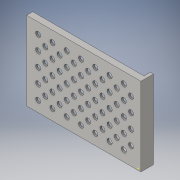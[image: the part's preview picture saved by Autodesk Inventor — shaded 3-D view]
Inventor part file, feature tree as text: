
AUTODESK INVENTOR PART (.ipt)
format: ipt  version: 2016 (Build 200138000, 138)  size: 350,208 bytes
history: native  units: mm
features: sketch x19, extrude x17
ambient origin geometry x8: Origin, YZ Plane, XZ Plane, XY Plane, X Axis, Y Axis, Z Axis, Center Point
bodies: Solid1 (feature_tree)
feature tree (36):
  extrude  "Extrusion1"  Depth=63.0mm
  extrude  "Extrusion2"  Depth=7.5mm
  sketch  "Sketch5"  dims[d4=7.5mm d11=4.3mm]
  extrude  "Extrusion3"  Depth=4.3mm
  sketch  "Sketch7"  dims[d19=1.5mm d20=0.0mm d24=3.612mm d25=0.0mm]
  extrude  "Extrusion4"  Depth=3.0mm
  extrude  "Extrusion5"  Depth=1.5mm TaperAngle=0.0deg
  extrude  "Extrusion6"  Depth=1.5mm
  extrude  "Extrusion7"  Depth=97.5mm
  extrude  "Extrusion8"  Depth=0.5mm TaperAngle=0.0deg
  extrude  "Extrusion9"  Depth=0.5mm TaperAngle=0.0deg
  extrude  "Extrusion10"  Depth=3.0mm TaperAngle=0.0deg
  extrude  "Extrusion11"  Depth=1.5mm
  extrude  "Extrusion12"  Depth=66.0mm
  extrude  "Extrusion13"  Depth=3.0mm TaperAngle=0.0deg
  extrude  "Extrusion14"  Depth=3.0mm
  extrude  "Extrusion15"  Depth=3.0mm
  extrude  "Extrusion16"  Depth=9.0mm TaperAngle=0.0deg
  extrude  "Extrusion17"  Depth=3.65mm TaperAngle=0.0deg
  sketch  "Sketch1"  dims[d0=91.5mm d1=63.0mm]
  sketch  "Sketch2"  dims[d2=4.3mm d3=7.5mm]
  sketch  "Sketch6"  dims[d17=3.0mm d18=3.0mm]
  sketch  "Sketch8"  dims[d26=1.5mm d27=0.0mm d30=97.5mm]
  sketch  "Sketch9"  dims[d31=69.0mm d32=97.5mm]
  sketch  "Sketch10"  dims[d33=5.388mm d34=0.0mm d35=0.5mm d36=0.0mm]
  sketch  "Sketch11"  dims[d37=0.5mm d38=0.0mm d39=0.5mm d40=0.0mm]
  sketch  "Sketch12"  dims[d41=3.0mm d42=0.0mm d43=3.0mm d44=0.0mm]
  sketch  "Sketch13"  dims[d45=0.75mm d46=1.5mm]
  sketch  "Sketch14"  dims[d47=96.0mm d48=66.0mm]
  sketch  "Sketch15"  dims[d49=3.0mm d50=0.0mm d51=3.0mm d52=0.0mm]
  sketch  "Sketch16"  dims[d53=3.0mm d54=0.0mm d55=3.0mm]
  sketch  "Sketch17"  dims[d56=5.0mm d57=3.0mm]
  sketch  "Sketch18"  dims[d58=5.0mm d59=9.0mm d60=0.0mm]
  sketch  "Sketch19"  dims[d61=1.5mm d64=3.65mm d65=0.0mm]
  sketch  "Sketch20"  dims[d66=0.5mm d67=0.0mm]
  sketch  "Sketch21"  dims[d68=0.5mm d69=0.0mm d70=0.5mm d71=0.0mm d72=0.5mm d73=0.0mm]
